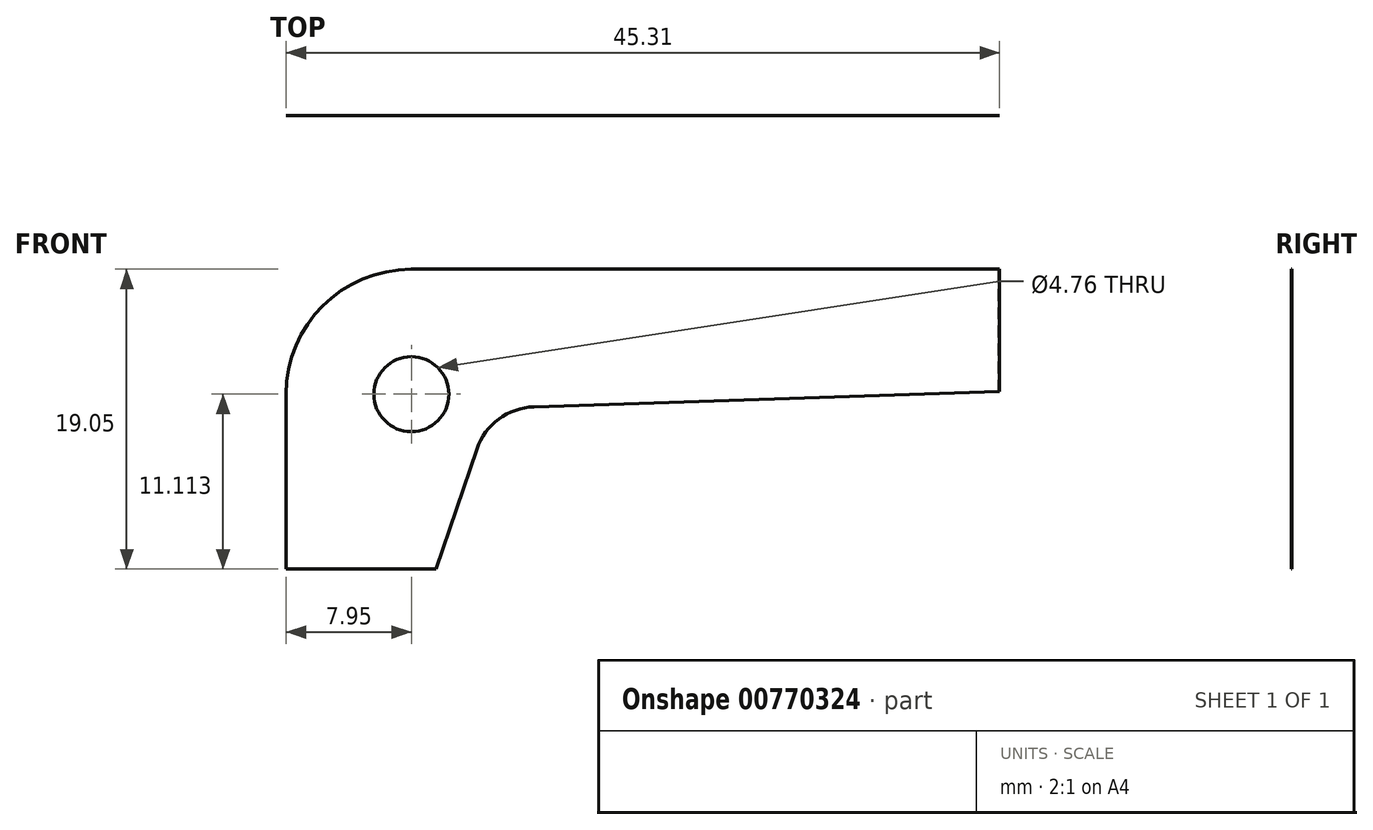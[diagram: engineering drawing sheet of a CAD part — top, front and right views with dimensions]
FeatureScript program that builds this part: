
annotation { "Feature Type Name" : "Feature", "Feature Type Description" : "" }
export const myFeature = defineFeature(function(context is Context, id is Id, definition is map)
    precondition{}
    {
        {
            var Q0;
            Q0=qCreatedBy(makeId("Front.planeOp"),FACE);
            var sketch = newSketch(context, id + "F0", { "sketchPlane" : qUnion([Q0])});
            skLineSegment(sketch, "E0.top", {"start": v(7.94, 19.05) * mm, "end": v(60.33, 19.05) * mm});
            skLineSegment(sketch, "E0.left", {"start": v(0, 0) * mm, "end": v(0, 11.11) * mm});
            skLineSegment(sketch, "E1", {"start": v(9.53, 0) * mm, "end": v(12.12, 7.63) * mm});
            skLineSegment(sketch, "E2", {"start": v(60.33, 11.77) * mm, "end": v(15.75, 10.32) * mm});
            skLineSegment(sketch, "E3", {"start": v(9.53, 0) * mm, "end": v(0, 0) * mm});
            skLineSegment(sketch, "E4", {"start": v(60.33, 11.77) * mm, "end": v(60.33, 19.05) * mm});
            skArc(sketch, "E5", {"start": v(15.75, 10.32) * mm, "mid": v(13.51, 9.54) * mm, "end": v(12.12, 7.63) * mm});
            skPoint(sketch, "E6.visualSharp", {"position": v(0, 19.05) * mm});
            skArc(sketch, "E6.filletArc", {"start": v(7.94, 19.05) * mm, "mid": v(2.32, 16.73) * mm, "end": v(0, 11.11) * mm});
            skSolve(sketch);
        }
        {
            var Q0;
            Q0=makeQuery(id+"F0.imprint","IMPRINT",FACE,{"disambiguationData":[TD([[makeQuery(id+"F0.imprint","IMPRINT",EDGE,{"derivedFrom":sQuery(id+"F0.wireOp",EDGE,"E0.top")}),-1.0]])]});
            extrude(context, id + "F1", {"entities" : qUnion([Q0]), "depth" : 3 / 812.8 * mm, "offsetDistance" : 25.4 * mm});
        }
        {
            var Q0;
            Q0=makeQuery(id+"F1.opExtrude","CAP_FACE",FACE,{"disambiguationData":[OSD([sQuery(id+"F0.wireOp",EDGE,"E0.top"),sQuery(id+"F0.wireOp",EDGE,"E0.left"),sQuery(id+"F0.wireOp",EDGE,"E1"),sQuery(id+"F0.wireOp",EDGE,"E2"),sQuery(id+"F0.wireOp",EDGE,"E3"),sQuery(id+"F0.wireOp",EDGE,"E4"),sQuery(id+"F0.wireOp",EDGE,"E5"),sQuery(id+"F0.wireOp",EDGE,"E6.filletArc")])],"isStart":false});
            var sketch = newSketch(context, id + "F2", { "sketchPlane" : qUnion([Q0])});
            skCircle(sketch, "E7", {"center": v(7.95, 11.11) * mm, "radius": 2.38 * mm});
            skSolve(sketch);
        }
        {
            var Q0;
            Q0=makeQuery(id+"F2.imprint","IMPRINT",FACE,{"disambiguationData":[TD([[makeQuery(id+"F2.imprint","IMPRINT",EDGE,{"derivedFrom":sQuery(id+"F2.wireOp",EDGE,"E7")}),1.0]])]});
            extrude(context, id + "F3", {"entities" : qUnion([Q0]), "operationType" : NewBodyOperationType.REMOVE, "oppositeDirection" : true, "depth" : 25.4 * mm, "offsetDistance" : 25.4 * mm});
        }
        {
            var Q0;
            Q0=makeQuery(id+"F1.opExtrude","SWEPT_FACE",FACE,{"disambiguationData":[OSD([sQuery(id+"F0.wireOp",EDGE,"E0.top")])]});
            var sketch = newSketch(context, id + "F4", { "sketchPlane" : qUnion([Q0])});
            skLineSegment(sketch, "E8", {"start": v(60.33, -0.8) * mm, "end": v(45.24, 0) * mm});
            skLineSegment(sketch, "E9", {"start": v(60.33, -1.2) * mm, "end": v(41.97, -1.2) * mm});
            skLineSegment(sketch, "E10.MirrorCS", {"start": v(60.33, -1.59) * mm, "end": v(45.24, -2.38) * mm});
            skSolve(sketch);
        }
        {
            var Q0;
            {var subQ0=sQuery(id+"F4.wireOp",EDGE,"E8");Q0=makeQuery(id+"F4.imprint","IMPRINT",FACE,{"disambiguationData":[TD([[makeQuery(id+"F4.imprint","IMPRINT",EDGE,{"derivedFrom":subQ0}),-1.0]])]});}
            var Q1;
            {var subQ0=sQuery(id+"F4.wireOp",EDGE,"E10.MirrorCS");Q1=makeQuery(id+"F4.imprint","IMPRINT",FACE,{"disambiguationData":[TD([[makeQuery(id+"F4.imprint","IMPRINT",EDGE,{"derivedFrom":subQ0}),1.0]])]});}
            extrude(context, id + "F5", {"entities" : qUnion([Q0, Q1]), "operationType" : NewBodyOperationType.REMOVE, "oppositeDirection" : true, "depth" : 25.4 * mm, "offsetDistance" : 25.4 * mm});
        }
    });
